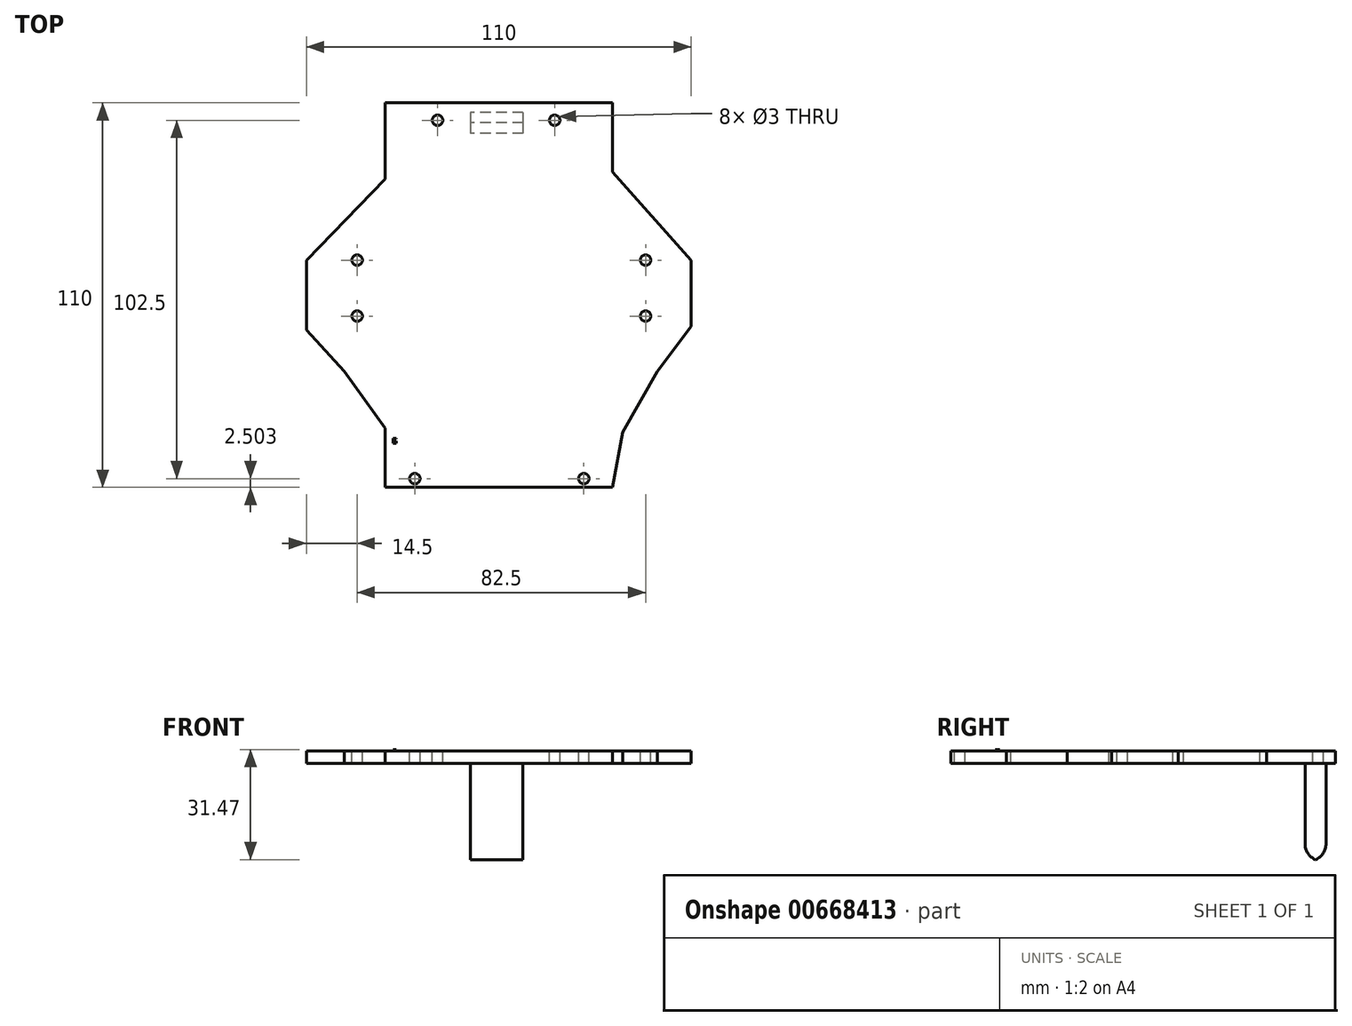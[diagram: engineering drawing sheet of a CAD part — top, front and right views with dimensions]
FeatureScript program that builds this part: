
annotation { "Feature Type Name" : "Feature", "Feature Type Description" : "" }
export const myFeature = defineFeature(function(context is Context, id is Id, definition is map)
    precondition{}
    {
        {
            var Q0;
            Q0=qCreatedBy(makeId("Top.planeOp"),FACE);
            var sketch = newSketch(context, id + "F0", { "sketchPlane" : qUnion([Q0])});
            skLineSegment(sketch, "E0", {"start": v(-32.5, 70.65) * mm, "end": v(32.5, 70.65) * mm});
            skLineSegment(sketch, "E1", {"start": v(-32.5, -39.35) * mm, "end": v(32.5, -39.35) * mm});
            skLineSegment(sketch, "E2.left", {"start": v(-55, 25.65) * mm, "end": v(-55, 5.65) * mm});
            skLineSegment(sketch, "E2.right", {"start": v(55, 25.65) * mm, "end": v(55, 6.63) * mm});
            skLineSegment(sketch, "E3", {"start": v(-32.5, 70.65) * mm, "end": v(-32.5, 59.42) * mm});
            skLineSegment(sketch, "E4", {"start": v(-32.5, 59.42) * mm, "end": v(-32.5, 48.88) * mm});
            skLineSegment(sketch, "E5", {"start": v(-32.5, 48.88) * mm, "end": v(-55, 25.65) * mm});
            skLineSegment(sketch, "E6", {"start": v(32.5, 70.65) * mm, "end": v(32.5, 50.88) * mm});
            skLineSegment(sketch, "E7", {"start": v(32.5, 50.88) * mm, "end": v(55, 25.65) * mm});
            skLineSegment(sketch, "E8", {"start": v(-55, 5.65) * mm, "end": v(-44.14, -6.1) * mm});
            skLineSegment(sketch, "E9", {"start": v(-44.14, -6.1) * mm, "end": v(-32.5, -22.36) * mm});
            skLineSegment(sketch, "E10", {"start": v(-32.5, -22.36) * mm, "end": v(-32.5, -39.35) * mm});
            skLineSegment(sketch, "E11", {"start": v(55, 6.63) * mm, "end": v(45.3, -6.1) * mm});
            skLineSegment(sketch, "E12", {"start": v(45.3, -6.1) * mm, "end": v(35.46, -23.5) * mm});
            skLineSegment(sketch, "E13", {"start": v(35.46, -23.5) * mm, "end": v(32.5, -39.35) * mm});
            skSolve(sketch);
        }
        {
            var Q0;
            Q0=qCreatedBy(makeId("Top.planeOp"),FACE);
            var sketch = newSketch(context, id + "F1", { "sketchPlane" : qUnion([Q0])});
            skSolve(sketch);
        }
        {
            var Q0;
            Q0 = qSketchRegion(id + "F1", true);
            var Q1;
            Q1 = qSketchRegion(id + "F0", true);
            extrude(context, id + "F2", {"entities" : qUnion([Q0, Q1]), "depth" : 3.5 * mm, "offsetDistance" : 25 * mm});
        }
        {
            var Q0;
            Q0=makeQuery(id+"F2.opExtrude","CAP_FACE",FACE,{"disambiguationData":[OSD([sQuery(id+"F0.wireOp",EDGE,"E0"),sQuery(id+"F0.wireOp",EDGE,"E1"),sQuery(id+"F0.wireOp",EDGE,"E2.left"),sQuery(id+"F0.wireOp",EDGE,"E2.right"),sQuery(id+"F0.wireOp",EDGE,"E3"),sQuery(id+"F0.wireOp",EDGE,"E4"),sQuery(id+"F0.wireOp",EDGE,"E5"),sQuery(id+"F0.wireOp",EDGE,"E6"),sQuery(id+"F0.wireOp",EDGE,"E7"),sQuery(id+"F0.wireOp",EDGE,"E8"),sQuery(id+"F0.wireOp",EDGE,"E9"),sQuery(id+"F0.wireOp",EDGE,"E10"),sQuery(id+"F0.wireOp",EDGE,"E11"),sQuery(id+"F0.wireOp",EDGE,"E12"),sQuery(id+"F0.wireOp",EDGE,"E13")])],"isStart":false});
            var sketch = newSketch(context, id + "F3", { "sketchPlane" : qUnion([Q0])});
            skCircle(sketch, "E14", {"center": v(-17.5, 65.65) * mm, "radius": 1.5 * mm});
            skCircle(sketch, "E15", {"center": v(16, 65.65) * mm, "radius": 1.5 * mm});
            skCircle(sketch, "E16", {"center": v(-40.5, 25.65) * mm, "radius": 1.5 * mm});
            skCircle(sketch, "E17", {"center": v(-40.5, 9.65) * mm, "radius": 1.5 * mm});
            skCircle(sketch, "E18", {"center": v(42, 25.65) * mm, "radius": 1.5 * mm});
            skCircle(sketch, "E19", {"center": v(42, 9.65) * mm, "radius": 1.5 * mm});
            skCircle(sketch, "E20", {"center": v(24.32, -36.85) * mm, "radius": 1.5 * mm});
            skCircle(sketch, "E21", {"center": v(-24, -36.85) * mm, "radius": 1.5 * mm});
            skSolve(sketch);
        }
        {
            var Q0;
            Q0 = qSketchRegion(id + "F3", true);
            extrude(context, id + "F4", {"entities" : qUnion([Q0]), "operationType" : NewBodyOperationType.REMOVE, "oppositeDirection" : true, "depth" : 25 * mm, "offsetDistance" : 25 * mm});
        }
        {
            var Q0;
            Q0=makeQuery(id+"F0.imprint","IMPRINT",FACE,{"disambiguationData":[TD([[makeQuery(id+"F0.imprint","IMPRINT",EDGE,{"derivedFrom":sQuery(id+"F0.wireOp",EDGE,"E0")}),-1.0]])]});
            var sketch = newSketch(context, id + "F5", { "sketchPlane" : qUnion([Q0])});
            skLineSegment(sketch, "E22.bottom", {"start": v(6.9, 67.92) * mm, "end": v(-8.1, 67.92) * mm});
            skLineSegment(sketch, "E22.top", {"start": v(6.9, 61.92) * mm, "end": v(-8.1, 61.92) * mm});
            skLineSegment(sketch, "E22.left", {"start": v(6.9, 67.92) * mm, "end": v(6.9, 61.92) * mm});
            skLineSegment(sketch, "E22.right", {"start": v(-8.1, 67.92) * mm, "end": v(-8.1, 61.92) * mm});
            skSolve(sketch);
        }
        {
            var Q0;
            Q0=makeQuery(id+"F5.imprint","IMPRINT",FACE,{"disambiguationData":[TD([[makeQuery(id+"F5.imprint","IMPRINT",EDGE,{"derivedFrom":sQuery(id+"F5.wireOp",EDGE,"E22.bottom")}),1.0]])]});
            extrude(context, id + "F6", {"entities" : qUnion([Q0]), "operationType" : NewBodyOperationType.ADD, "oppositeDirection" : true, "depth" : 28 * mm, "offsetDistance" : 25 * mm});
        }
        {
            var Q0;
            Q0=makeQuery(id+"F6.opExtrude","CAP_EDGE",EDGE,{"disambiguationData":[OSD([sQuery(id+"F5.wireOp",EDGE,"E22.top")])],"isStart":false});
            var Q1;
            Q1=makeQuery(id+"F6.opExtrude","CAP_EDGE",EDGE,{"disambiguationData":[OSD([sQuery(id+"F5.wireOp",EDGE,"E22.bottom")])],"isStart":false});
            fillet(context, id + "F7", {"entities" : qUnion([Q0, Q1]), "radius" : 5 * mm, "tangentPropagation" : true, "allowEdgeOverflow" : false});
        }
        {
            var Q0;
            Q0=makeQuery(id+"F2.opExtrude","CAP_FACE",FACE,{"disambiguationData":[OSD([sQuery(id+"F0.wireOp",EDGE,"E0"),sQuery(id+"F0.wireOp",EDGE,"E1"),sQuery(id+"F0.wireOp",EDGE,"E2.left"),sQuery(id+"F0.wireOp",EDGE,"E2.right"),sQuery(id+"F0.wireOp",EDGE,"E3"),sQuery(id+"F0.wireOp",EDGE,"E4"),sQuery(id+"F0.wireOp",EDGE,"E5"),sQuery(id+"F0.wireOp",EDGE,"E6"),sQuery(id+"F0.wireOp",EDGE,"E7"),sQuery(id+"F0.wireOp",EDGE,"E8"),sQuery(id+"F0.wireOp",EDGE,"E9"),sQuery(id+"F0.wireOp",EDGE,"E10"),sQuery(id+"F0.wireOp",EDGE,"E11"),sQuery(id+"F0.wireOp",EDGE,"E12"),sQuery(id+"F0.wireOp",EDGE,"E13")])],"isStart":false});
            var sketch = newSketch(context, id + "F8", { "sketchPlane" : qUnion([Q0])});
            skLineSegment(sketch, "E23.bottom", {"start": v(-30.21, -25.5) * mm, "end": v(-29.91, -25.5) * mm});
            skLineSegment(sketch, "E23.top", {"start": v(-30.21, -26.7) * mm, "end": v(-29.91, -26.7) * mm});
            skLineSegment(sketch, "E23.left", {"start": v(-30.21, -25.5) * mm, "end": v(-30.21, -26.7) * mm});
            skLineSegment(sketch, "E23.right", {"start": v(-29.91, -25.5) * mm, "end": v(-29.91, -26.7) * mm});
            skLineSegment(sketch, "E24.bottom", {"start": v(-29.91, -26.1) * mm, "end": v(-29.31, -26.1) * mm});
            skLineSegment(sketch, "E24.top", {"start": v(-29.91, -26.7) * mm, "end": v(-29.31, -26.7) * mm});
            skLineSegment(sketch, "E24.left", {"start": v(-29.91, -26.1) * mm, "end": v(-29.91, -26.7) * mm});
            skLineSegment(sketch, "E24.right", {"start": v(-29.31, -26.1) * mm, "end": v(-29.31, -26.7) * mm});
            skLineSegment(sketch, "E25.bottom", {"start": v(-30.21, -25.5) * mm, "end": v(-30.01, -25.5) * mm});
            skLineSegment(sketch, "E26.bottom", {"start": v(-30.21, -25.5) * mm, "end": v(-29.31, -25.5) * mm});
            skLineSegment(sketch, "E26.top", {"start": v(-30.21, -25.36) * mm, "end": v(-29.31, -25.36) * mm});
            skLineSegment(sketch, "E26.left", {"start": v(-30.21, -25.5) * mm, "end": v(-30.21, -25.36) * mm});
            skLineSegment(sketch, "E26.right", {"start": v(-29.31, -25.5) * mm, "end": v(-29.31, -25.36) * mm});
            skSolve(sketch);
        }
        {
            var Q0;
            Q0 = qSketchRegion(id + "F8", true);
            extrude(context, id + "F9", {"entities" : qUnion([Q0]), "operationType" : NewBodyOperationType.ADD, "depth" : 0.39 * mm, "offsetDistance" : 25 * mm});
        }
    });
